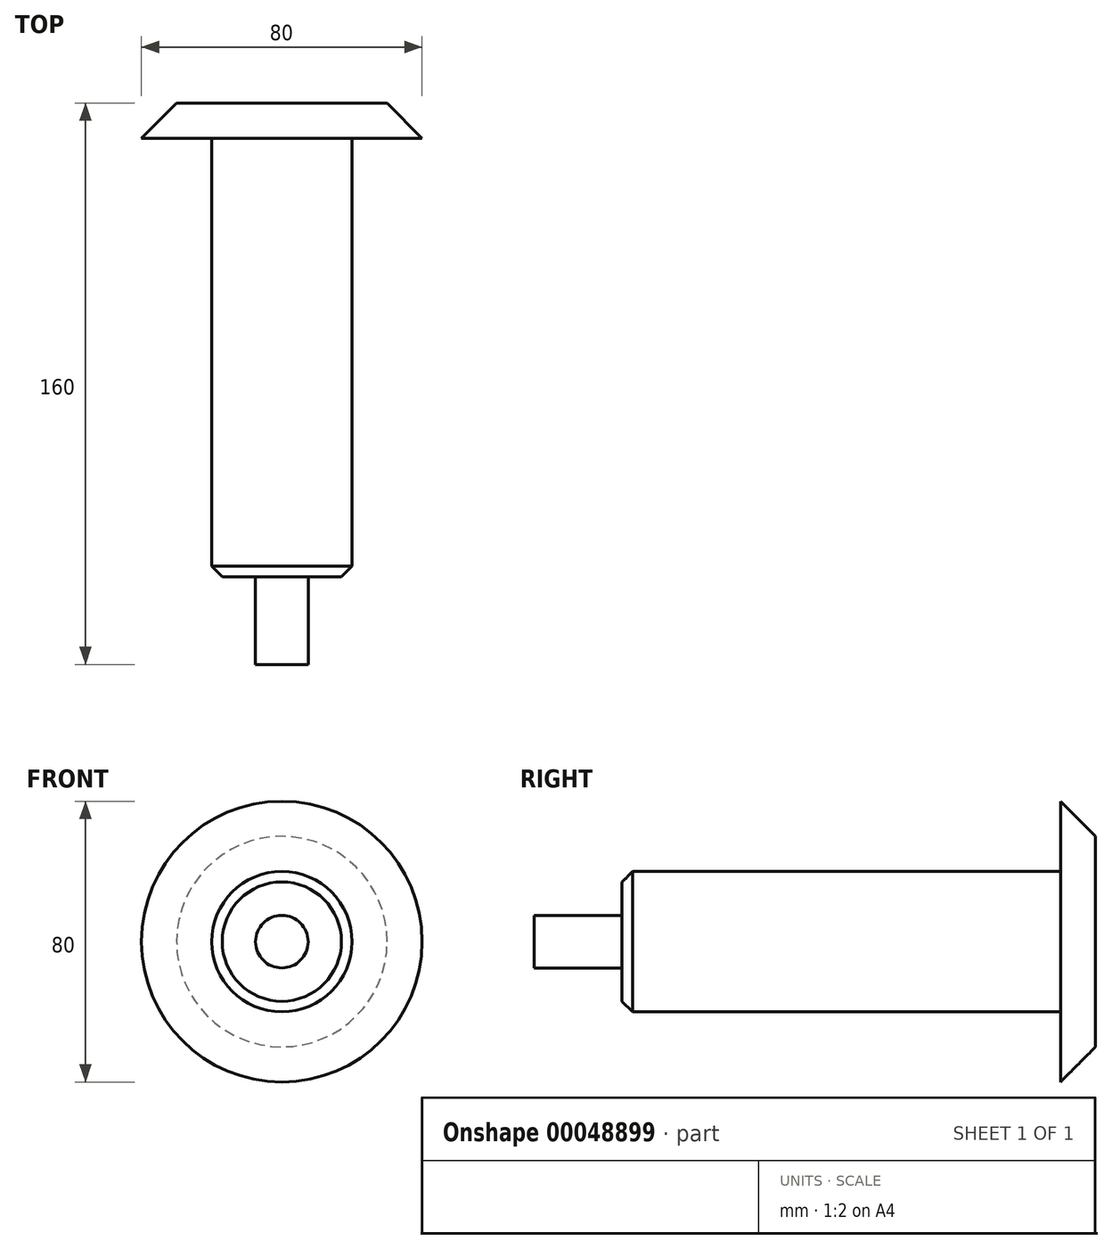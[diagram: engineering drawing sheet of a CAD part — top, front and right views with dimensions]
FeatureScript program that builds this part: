
annotation { "Feature Type Name" : "Feature", "Feature Type Description" : "" }
export const myFeature = defineFeature(function(context is Context, id is Id, definition is map)
    precondition{}
    {
        {
            var Q0;
            Q0=qCreatedBy(makeId("Right.planeOp"),FACE);
            var sketch = newSketch(context, id + "F0", { "sketchPlane" : qUnion([Q0])});
            skLineSegment(sketch, "E0", {"start": v(160, 0) * mm, "end": v(160, 40) * mm});
            skLineSegment(sketch, "E1", {"start": v(160, 40) * mm, "end": v(150, 40) * mm});
            skLineSegment(sketch, "E2", {"start": v(150, 40) * mm, "end": v(150, 20) * mm});
            skLineSegment(sketch, "E3", {"start": v(150, 20) * mm, "end": v(25, 20) * mm});
            skLineSegment(sketch, "E4", {"start": v(25, 20) * mm, "end": v(25, 7.5) * mm});
            skLineSegment(sketch, "E5", {"start": v(25, 7.5) * mm, "end": v(0, 7.5) * mm});
            skLineSegment(sketch, "E6", {"start": v(0, 7.5) * mm, "end": v(0, 0) * mm});
            skLineSegment(sketch, "E7", {"start": v(0, 0) * mm, "end": v(160, 0) * mm});
            skSolve(sketch);
        }
        {
            var Q0;
            Q0=makeQuery(id+"F0.imprint","IMPRINT",FACE,{"disambiguationData":[TD([[makeQuery(id+"F0.imprint","IMPRINT",EDGE,{"derivedFrom":sQuery(id+"F0.wireOp",EDGE,"E0")}),1.0]])]});
            var Q1;
            Q1=sQuery(id+"F0.wireOp",EDGE,"E7");
            revolve(context, id + "F1", {"entities" : qUnion([Q0]), "axis" : qUnion([Q1]), "revolveType" : RevolveType.FULL});
        }
        {
            var Q0;
            Q0=makeQuery(id+"F1.opRevolve","SWEPT_EDGE",EDGE,{"disambiguationData":[OSD([sQuery(id+"F0.wireOp",EDGE,"E0"),sQuery(id+"F0.wireOp",EDGE,"E1")])]});
            chamfer(context, id + "F2", {"entities" : qUnion([Q0]), "chamferType" : ChamferType.OFFSET_ANGLE, "width" : 10 * mm, "oppositeDirection" : false, "angle" : 45 * degree, "tangentPropagation" : true});
        }
        {
            var Q0;
            Q0=makeQuery(id+"F1.opRevolve","SWEPT_EDGE",EDGE,{"disambiguationData":[OSD([sQuery(id+"F0.wireOp",EDGE,"E3"),sQuery(id+"F0.wireOp",EDGE,"E4")])]});
            chamfer(context, id + "F3", {"entities" : qUnion([Q0]), "chamferType" : ChamferType.OFFSET_ANGLE, "width" : 3 * mm, "oppositeDirection" : false, "angle" : 45 * degree, "tangentPropagation" : true});
        }
    });
